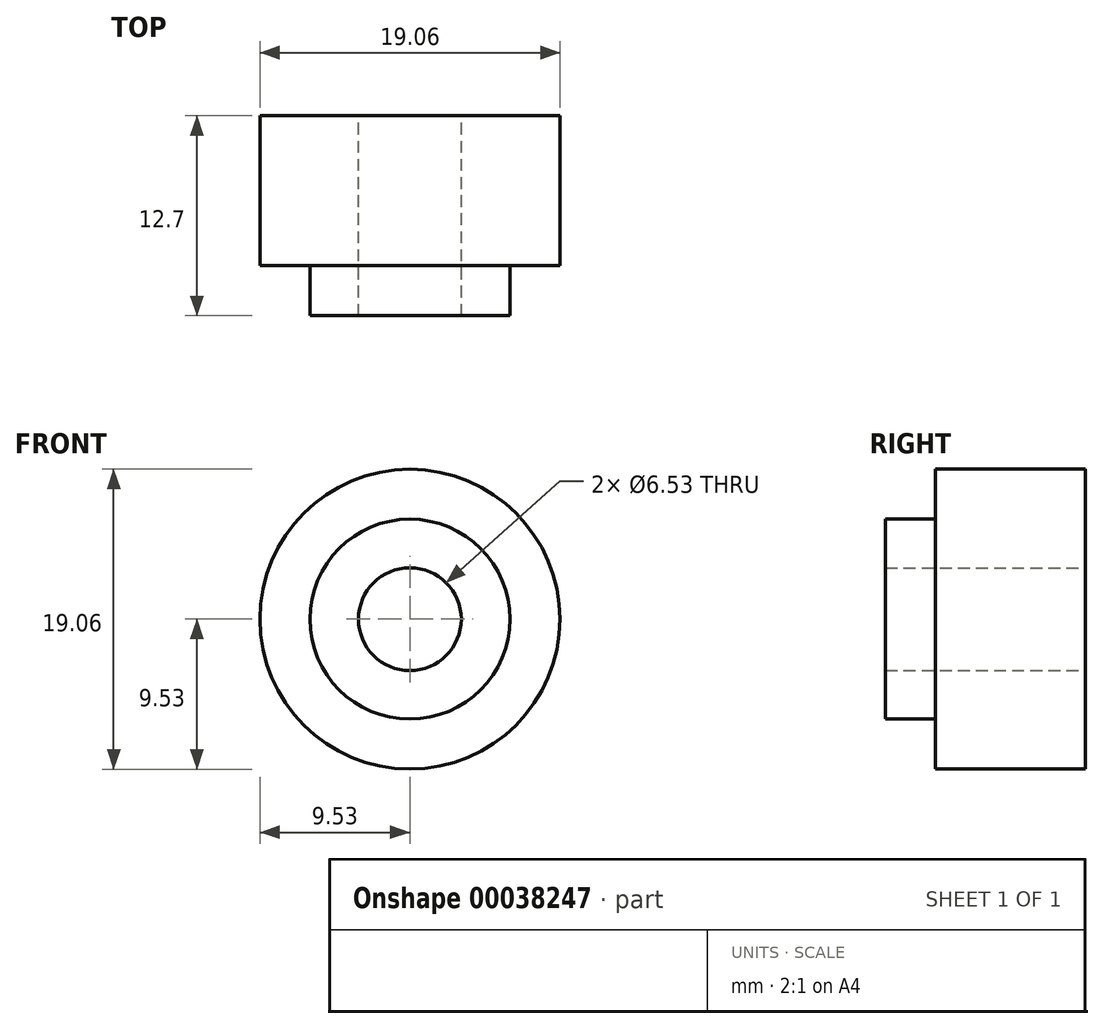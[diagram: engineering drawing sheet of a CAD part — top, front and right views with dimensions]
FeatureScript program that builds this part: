
annotation { "Feature Type Name" : "Feature", "Feature Type Description" : "" }
export const myFeature = defineFeature(function(context is Context, id is Id, definition is map)
    precondition{}
    {
        {
            var Q0;
            Q0=qCreatedBy(makeId("Front.planeOp"),FACE);
            var sketch = newSketch(context, id + "F0", { "sketchPlane" : qUnion([Q0])});
            skCircle(sketch, "E0", {"center": v(0, 0) * mm, "radius": 9.53 * mm});
            skCircle(sketch, "E1", {"center": v(0, 0) * mm, "radius": 3.26 * mm});
            skSolve(sketch);
        }
        {
            var Q0;
            Q0 = qSketchRegion(id + "F0", true);
            var Q1;
            Q1=makeQuery(id+"F0.imprint","IMPRINT",FACE,{"disambiguationData":[TD([[makeQuery(id+"F0.imprint","IMPRINT",EDGE,{"derivedFrom":sQuery(id+"F0.wireOp",EDGE,"E0")}),1.0]])]});
            extrude(context, id + "F1", {"entities" : qUnion([Q0, Q1]), "depth" : 12.7 * mm});
        }
        {
            var Q0;
            Q0=makeQuery(id+"F1.opExtrude","CAP_FACE",FACE,{"disambiguationData":[OSD([sQuery(id+"F0.wireOp",EDGE,"E0"),sQuery(id+"F0.wireOp",EDGE,"E1")])],"isStart":false});
            var sketch = newSketch(context, id + "F2", { "sketchPlane" : qUnion([Q0])});
            skCircle(sketch, "E2", {"center": v(0, 0) * mm, "radius": 6.35 * mm});
            skSolve(sketch);
        }
        {
            var Q0;
            Q0=makeQuery(id+"F2.imprint","IMPRINT",FACE,{"disambiguationData":[TD([[makeQuery(id+"F2.imprint","IMPRINT",EDGE,{"derivedFrom":sQuery(id+"F2.wireOp",EDGE,"E2")}),-1.0]])]});
            extrude(context, id + "F3", {"entities" : qUnion([Q0]), "operationType" : NewBodyOperationType.REMOVE, "oppositeDirection" : true, "depth" : 3.17 * mm});
        }
    });
